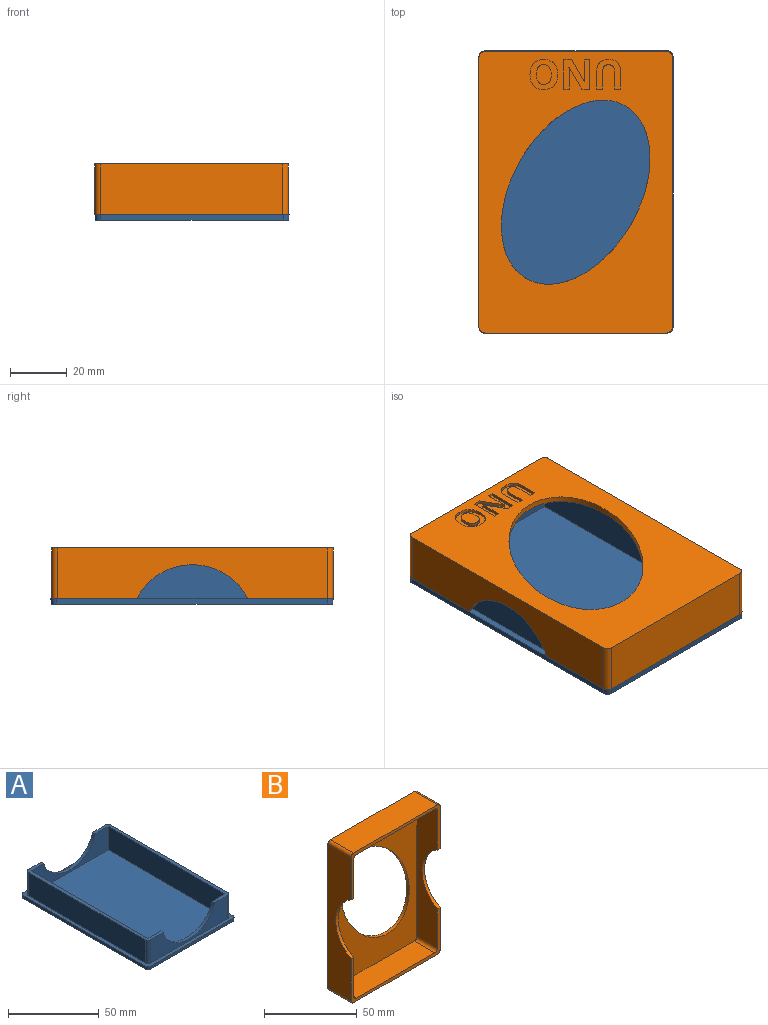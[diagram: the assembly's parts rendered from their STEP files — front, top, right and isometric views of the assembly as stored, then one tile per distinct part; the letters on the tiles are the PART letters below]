
ASSEMBLY  parts=2 mates=1
PART A: 27 faces, bbox 68.2x99.2x21.3 mm
  f0: plane 95x12mm, normal (0,0,1), area 228.3mm2, adj f1,f3,f4,f6,f7,f8,f21,f22
  f1: plane 60x21.26mm, normal (0,1,0), area 513.3mm2, adj f0,f2,f11,f22,f23,f25
  f2: plane 95x12mm, normal (0,0,1), area 228.3mm2, adj f1,f3,f5,f6,f8,f9,f23,f24
  f3: plane 60x21.2mm, normal (0,-1,0), area 513.3mm2, adj f0,f2,f11,f21,f24,f26
  f4: plane 91x15.7mm, normal (1,0,0), area 1428.7mm2, adj f0,f11,f21,f22
  f5: plane 91x15.7mm, normal (-1,0,0), area 1428.7mm2, adj f2,f11,f23,f24
  f6: plane 60x21.2mm, normal (0,1,0), area 513.3mm2, adj f0,f2,f7,f9,f10,f26
  f7: plane 91x15.7mm, normal (-1,0,0), area 1428.7mm2, adj f0,f6,f8,f10
  f8: plane 60x21.26mm, normal (0,-1,0), area 513.3mm2, adj f0,f2,f7,f9,f10,f25
  f9: plane 91x15.7mm, normal (1,0,0), area 1428.7mm2, adj f2,f6,f8,f10
  f10: plane 91x60mm, normal (0,0,1), area 5460mm2, adj f6,f7,f8,f9
  f11: plane 99.21x68.21mm, normal (0,0,1), area 687.1mm2, adj f1,f3,f4,f5,f12,f13,f14,f15
  f12: plane 64.22x2mm, normal (0,-1,-0.05), area 128.4mm2, adj f11,f16,f17,f20
  f13: plane 95.22x2mm, normal (1,0,-0.05), area 190.5mm2, adj f11,f16,f17,f18
  f14: plane 64.22x2mm, normal (0,1,-0.05), area 128.4mm2, adj f11,f16,f18,f19
  f15: plane 95.22x2mm, normal (-1,0,-0.05), area 190.5mm2, adj f11,f16,f19,f20
  f16: plane 99x68mm, normal (0,0,-1), area 6728.6mm2, adj f12,f13,f14,f15,f17,f18,f19,f20
  f17: cylinder r=2mm len=2.1mm, axis (-0.05,0.05,-1), area 6.3mm2, adj f11,f12,f13,f16
  f18: cylinder r=2mm len=2.1mm, axis (-0.05,-0.05,-1), area 6.3mm2, adj f11,f13,f14,f16
  f19: cylinder r=2mm len=2.1mm, axis (0.05,-0.05,-1), area 6.3mm2, adj f11,f14,f15,f16
  f20: cylinder r=2mm len=2.1mm, axis (0.05,0.05,-1), area 6.3mm2, adj f11,f12,f15,f16
  f21: cylinder r=2mm len=15.7mm, axis (0,0,1), area 49.3mm2, adj f0,f3,f4,f11
  f22: cylinder r=2mm len=15.7mm, axis (0,0,-1), area 49.3mm2, adj f0,f1,f4,f11
  f23: cylinder r=2mm len=15.7mm, axis (0,0,1), area 49.3mm2, adj f1,f2,f5,f11
  f24: cylinder r=2mm len=15.7mm, axis (0,0,-1), area 49.3mm2, adj f2,f3,f5,f11
  f25: extruded ~40x14.46mm, area 106mm2, adj f0,f1,f2,f8
  f26: extruded ~40x14.47mm, area 106mm2, adj f0,f2,f3,f6
PART B: 70 faces, bbox 68x17.7x99 mm
  f0: plane 68x30mm, normal (0,-1,0), area 248mm2, adj f2,f4,f6,f7,f8,f10,f13,f16
  f1: plane 68x30mm, normal (0,-1,0), area 248mm2, adj f2,f5,f6,f8,f9,f10,f14,f15
  f2: plane 95x17.7mm, normal (-1,0,0), area 1352.8mm2, adj f0,f1,f3,f17,f18,f68
  f3: plane 99x68mm, normal (0,1,0), area 4062.6mm2, adj f2,f4,f5,f6,f12,f17,f18,f19
  f4: plane 64x17.7mm, normal (0,0,1), area 1132.8mm2, adj f0,f3,f17,f20
  f5: plane 64x17.7mm, normal (0,0,-1), area 1132.8mm2, adj f1,f3,f18,f19
  f6: plane 95x17.7mm, normal (1,0,0), area 1352.8mm2, adj f0,f1,f3,f19,f20,f69
  f7: plane 60x15.7mm, normal (0,0,-1), area 942mm2, adj f0,f11,f13,f16
  f8: plane 91x15.7mm, normal (1,0,0), area 1100mm2, adj f0,f1,f11,f13,f14,f68
  f9: plane 60x15.7mm, normal (0,0,1), area 942mm2, adj f1,f11,f14,f15
  f10: plane 91x15.7mm, normal (-1,0,0), area 1100mm2, adj f0,f1,f11,f15,f16,f69
  f11: plane 95x64mm, normal (0,-1,0), area 3602.6mm2, adj f7,f8,f9,f10,f12,f13,f14,f15
  f12: extruded ~64.68x52.2mm, area 365.6mm2, adj f3,f11
  f13: cylinder r=2mm len=15.7mm, axis (0,-1,0), area 49.3mm2, adj f0,f7,f8,f11
  f14: cylinder r=2mm len=15.7mm, axis (0,1,0), area 49.3mm2, adj f1,f8,f9,f11
  f15: cylinder r=2mm len=15.7mm, axis (0,-1,0), area 49.3mm2, adj f1,f9,f10,f11
  f16: cylinder r=2mm len=15.7mm, axis (0,1,0), area 49.3mm2, adj f0,f7,f10,f11
  f17: cylinder r=2mm len=17.7mm, axis (0,-1,0), area 55.6mm2, adj f0,f2,f3,f4
  f18: cylinder r=2mm len=17.7mm, axis (0,1,0), area 55.6mm2, adj f1,f2,f3,f5
  f19: cylinder r=2mm len=17.7mm, axis (0,-1,0), area 55.6mm2, adj f1,f3,f5,f6
  f20: cylinder r=2mm len=17.7mm, axis (0,1,0), area 55.6mm2, adj f0,f3,f4,f6
  f21: extruded ~2.58x1mm, area 2.7mm2, adj f22,f34,f35,f67
  f22: extruded ~2.59x1mm, area 2.7mm2, adj f21,f23,f35,f67
  f23: extruded ~1.95x1mm, area 2.2mm2, adj f22,f24,f35,f67
  f24: extruded ~3.46x2.58mm, area 4.9mm2, adj f23,f25,f35,f67
  f25: extruded ~3.45x2.6mm, area 4.9mm2, adj f24,f34,f35,f67
  f26: extruded ~3.91x1.26mm, area 4.2mm2, adj f3,f27,f33,f35
  f27: extruded ~3.91x1.25mm, area 4.2mm2, adj f3,f26,f28,f35
  f28: extruded ~3.61x1.36mm, area 4mm2, adj f3,f27,f29,f35
  f29: extruded ~3.62x1.35mm, area 4mm2, adj f3,f28,f30,f35
  f30: extruded ~3.9x1.26mm, area 4.2mm2, adj f3,f29,f31,f35
  f31: extruded ~3.92x1.26mm, area 4.2mm2, adj f3,f30,f32,f35
  f32: extruded ~3.61x1.37mm, area 4mm2, adj f3,f31,f33,f35
  f33: extruded ~3.61x1.37mm, area 4mm2, adj f3,f26,f32,f35
  f34: extruded ~1.95x1mm, area 2.2mm2, adj f21,f25,f35,f67
  f35: plane 10.54x9.74mm, normal (0,1,0), area 54.9mm2, adj f21,f22,f23,f24,f25,f26,f27,f28
  f36: plane 2.76x1mm, normal (0,0,1), area 2.8mm2, adj f3,f37,f49,f50
  f37: plane 10.24x1mm, normal (1,0,0), area 10.2mm2, adj f3,f36,f38,f50
  f38: plane 1.95x1mm, normal (0,0,-1), area 2mm2, adj f3,f37,f39,f50
  f39: plane 4.85x1mm, normal (-1,0,0), area 4.8mm2, adj f3,f38,f40,f50
  f40: extruded ~2.82x1mm, area 2.8mm2, adj f3,f39,f41,f50
  f41: plane 1x0.05mm, normal (0,0,-1), area 0mm2, adj f3,f40,f42,f50
  f42: plane 7.67x4.44mm, normal (0.87,0,-0.5), area 8.9mm2, adj f3,f41,f43,f50
  f43: plane 2.74x1mm, normal (0,0,-1), area 2.7mm2, adj f3,f42,f44,f50
  f44: plane 10.24x1mm, normal (-1,0,0), area 10.2mm2, adj f3,f43,f45,f50
  f45: plane 1.94x1mm, normal (0,0,1), area 1.9mm2, adj f3,f44,f46,f50
  f46: plane 4.82x1mm, normal (1,0,0), area 4.8mm2, adj f3,f45,f47,f50
  f47: extruded ~2.93x1mm, area 2.9mm2, adj f3,f46,f48,f50
  f48: plane 1x0.06mm, normal (0,0,1), area 0.1mm2, adj f3,f47,f49,f50
  f49: plane 7.74x4.45mm, normal (-0.87,0,0.5), area 8.9mm2, adj f3,f36,f48,f50
  f50: plane 10.24x9.08mm, normal (0,1,0), area 59.4mm2, adj f36,f37,f38,f39,f40,f41,f42,f43
  f51: plane 6.62x1mm, normal (1,0,0), area 6.6mm2, adj f3,f52,f65,f66
  f52: plane 2.16x1mm, normal (0,0,-1), area 2.2mm2, adj f3,f51,f53,f66
  f53: plane 6.25x1mm, normal (-1,0,0), area 6.3mm2, adj f3,f52,f54,f66
  f54: extruded ~1.75x1mm, area 1.8mm2, adj f3,f53,f55,f66
  f55: extruded ~1.54x1mm, area 1.7mm2, adj f3,f54,f56,f66
  f56: extruded ~1.58x1mm, area 1.7mm2, adj f3,f55,f57,f66
  f57: extruded ~1.74x1mm, area 1.8mm2, adj f3,f56,f58,f66
  f58: plane 6.27x1mm, normal (1,0,0), area 6.3mm2, adj f3,f57,f59,f66
  f59: plane 2.16x1mm, normal (0,0,-1), area 2.2mm2, adj f3,f58,f60,f66
  f60: plane 6.6x1mm, normal (-1,0,0), area 6.6mm2, adj f3,f59,f61,f66
  f61: extruded ~2.77x1.09mm, area 3.1mm2, adj f3,f60,f62,f66
  f62: extruded ~3.07x1.01mm, area 3.3mm2, adj f3,f61,f63,f66
  f63: extruded ~2.27x1mm, area 2.3mm2, adj f3,f62,f64,f66
  f64: extruded ~1.47x1.31mm, area 2mm2, adj f3,f63,f65,f66
  f65: extruded ~1.99x1mm, area 2.1mm2, adj f3,f51,f64,f66
  f66: plane 10.38x8.4mm, normal (0,1,0), area 47.9mm2, adj f51,f52,f53,f54,f55,f56,f57,f58
  f67: plane 6.91x5.19mm, normal (0,1,0), area 29.9mm2, adj f21,f22,f23,f24,f25,f34
  f68: cylinder r=22mm len=39mm, axis (-1,0,0), area 95.9mm2, adj f0,f1,f2,f8
  f69: cylinder r=22mm len=39mm, axis (1,0,0), area 95.9mm2, adj f0,f1,f6,f10
PLACE A t=(2.54,1.53,-1.23)mm
PLACE B rot(axis=(1,0,0),90deg) t=(55.9,16.27,18.47)mm
MATE fastened B.f0 <-> A.f11  axis (0,0,1) through (-31.57,-46.08,0.77)mm
